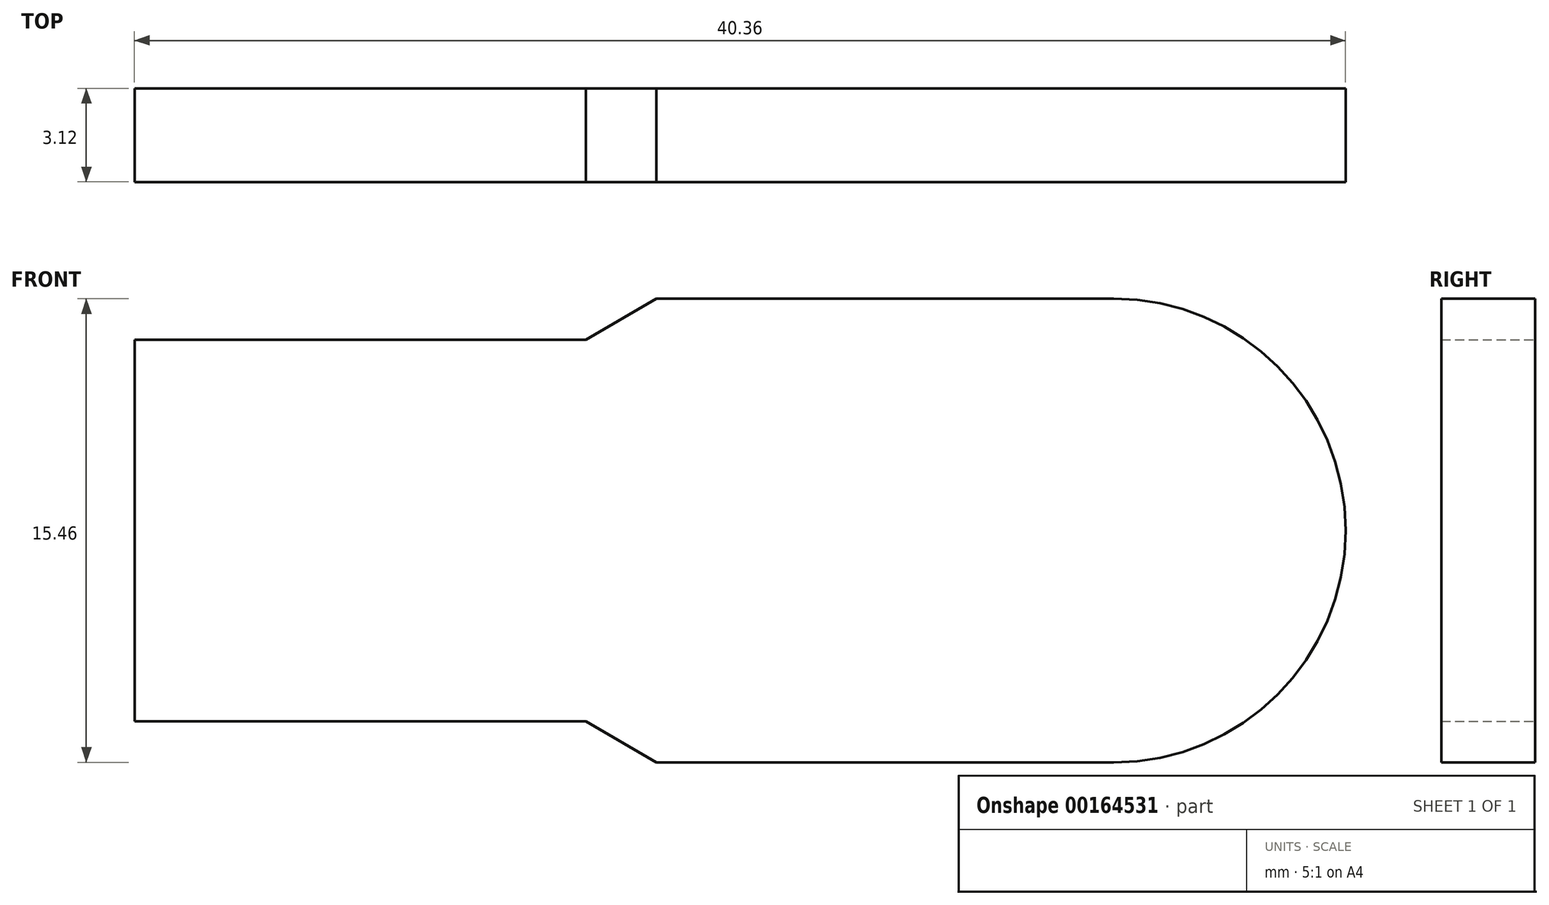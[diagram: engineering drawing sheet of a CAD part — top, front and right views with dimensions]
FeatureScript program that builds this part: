
annotation { "Feature Type Name" : "Feature", "Feature Type Description" : "" }
export const myFeature = defineFeature(function(context is Context, id is Id, definition is map)
    precondition{}
    {
        {
            var Q0;
            Q0=qCreatedBy(makeId("Front.planeOp"),FACE);
            var sketch = newSketch(context, id + "F0", { "sketchPlane" : qUnion([Q0])});
            skLineSegment(sketch, "E0.bottom", {"start": v(7.62, 7.73) * mm, "end": v(-7.62, 7.73) * mm});
            skLineSegment(sketch, "E0.top", {"start": v(7.62, -7.73) * mm, "end": v(-7.62, -7.73) * mm});
            skLineSegment(sketch, "E0.left", {"start": v(7.62, 7.73) * mm, "end": v(7.62, -7.73) * mm});
            skLineSegment(sketch, "E0.right", {"start": v(-7.62, 7.73) * mm, "end": v(-7.62, -7.73) * mm});
            skPoint(sketch, "E0.middle", {"position": v(0, 0) * mm});
            skArc(sketch, "E1", {"start": v(7.62, -7.73) * mm, "mid": v(15.35, 0) * mm, "end": v(7.62, 7.73) * mm});
            skLineSegment(sketch, "E2", {"start": v(-7.62, 7.73) * mm, "end": v(-20.81, 0) * mm});
            skLineSegment(sketch, "E3", {"start": v(-7.62, -7.73) * mm, "end": v(-20.81, 0) * mm});
            skLineSegment(sketch, "E4", {"start": v(-9.96, 6.36) * mm, "end": v(-22.66, 6.36) * mm});
            skLineSegment(sketch, "E5", {"start": v(-9.96, -6.36) * mm, "end": v(-22.66, -6.36) * mm});
            skLineSegment(sketch, "E6", {"start": v(-25, 6.36) * mm, "end": v(-25, -6.36) * mm});
            skPoint(sketch, "E7", {"position": v(-25, 0) * mm});
            skLineSegment(sketch, "E8", {"start": v(-22.66, 6.36) * mm, "end": v(-58.22, 6.36) * mm});
            skLineSegment(sketch, "E9", {"start": v(-58.22, 6.36) * mm, "end": v(-106.57, 0) * mm});
            skLineSegment(sketch, "E10", {"start": v(-22.66, -6.36) * mm, "end": v(-25, -6.36) * mm});
            skFitSpline(sketch, "E11", {"points": [v(-25, -6.36) * mm, v(-55.76, -6.36) * mm, v(-106.57, 0) * mm], "startDerivative": vector(-29.4, -1.01) * mm, "endDerivative": vector(-27.7, 19.91) * mm});
            skSolve(sketch);
        }
        {
            var Q0;
            {var subQ1=sQuery(id+"F0.wireOp",EDGE,"E0.right");Q0=makeQuery(id+"F0.imprint","IMPRINT",FACE,{"disambiguationData":[TD([[makeQuery(id+"F0.imprint","IMPRINT",EDGE,{"derivedFrom":subQ1}),-1.0]])]});}
            var Q1;
            Q1=makeQuery(id+"F0.imprint","IMPRINT",FACE,{"disambiguationData":[TD([[makeQuery(id+"F0.imprint","IMPRINT",EDGE,{"derivedFrom":sQuery(id+"F0.wireOp",EDGE,"E0.bottom")}),1.0]])]});
            var Q2;
            Q2=makeQuery(id+"F0.imprint","IMPRINT",FACE,{"disambiguationData":[TD([[makeQuery(id+"F0.imprint","IMPRINT",EDGE,{"derivedFrom":sQuery(id+"F0.wireOp",EDGE,"E0.left")}),1.0]])]});
            var Q3;
            {var subQ1=sQuery(id+"F0.wireOp",EDGE,"E4");Q3=makeQuery(id+"F0.imprint","IMPRINT",FACE,{"disambiguationData":[TD([[makeQuery(id+"F0.imprint","IMPRINT",EDGE,{"derivedFrom":subQ1}),1.0]])]});}
            extrude(context, id + "F1", {"entities" : qUnion([Q0, Q1, Q2, Q3]), "depth" : 3.12 * mm});
        }
        {
            var Q0;
            Q0=sQuery(id+"F0.wireOp",EDGE,"E8");
            var Q1;
            Q1=sQuery(id+"F0.wireOp",EDGE,"E9");
            extrude(context, id + "F2", {"bodyType" : ToolBodyType.SURFACE, "surfaceEntities" : qUnion([Q0, Q1]), "depth" : 3.12 * mm});
        }
    });
